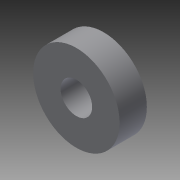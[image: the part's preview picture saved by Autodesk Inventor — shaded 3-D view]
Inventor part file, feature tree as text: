
AUTODESK INVENTOR PART (.ipt)
format: ipt  version: 2015 (Build 190159000, 159)  size: 78,336 bytes
history: native  units: in
note: dims shown in document units (in); Inventor stores cm internally (conversion verified against a paired STEP export)
features: extrude x1, sketch x1
ambient origin geometry x8: Origin, YZ Plane, XZ Plane, XY Plane, X Axis, Y Axis, Z Axis, Center Point
bodies: Solid1 (feature_tree)
feature tree (2):
  extrude  "Extrusion1"  Depth=0.2717in
  sketch  "Sketch1"  dims[d0=0.315in d1=0.8622in d2=0.2717in d3=0.0in]
